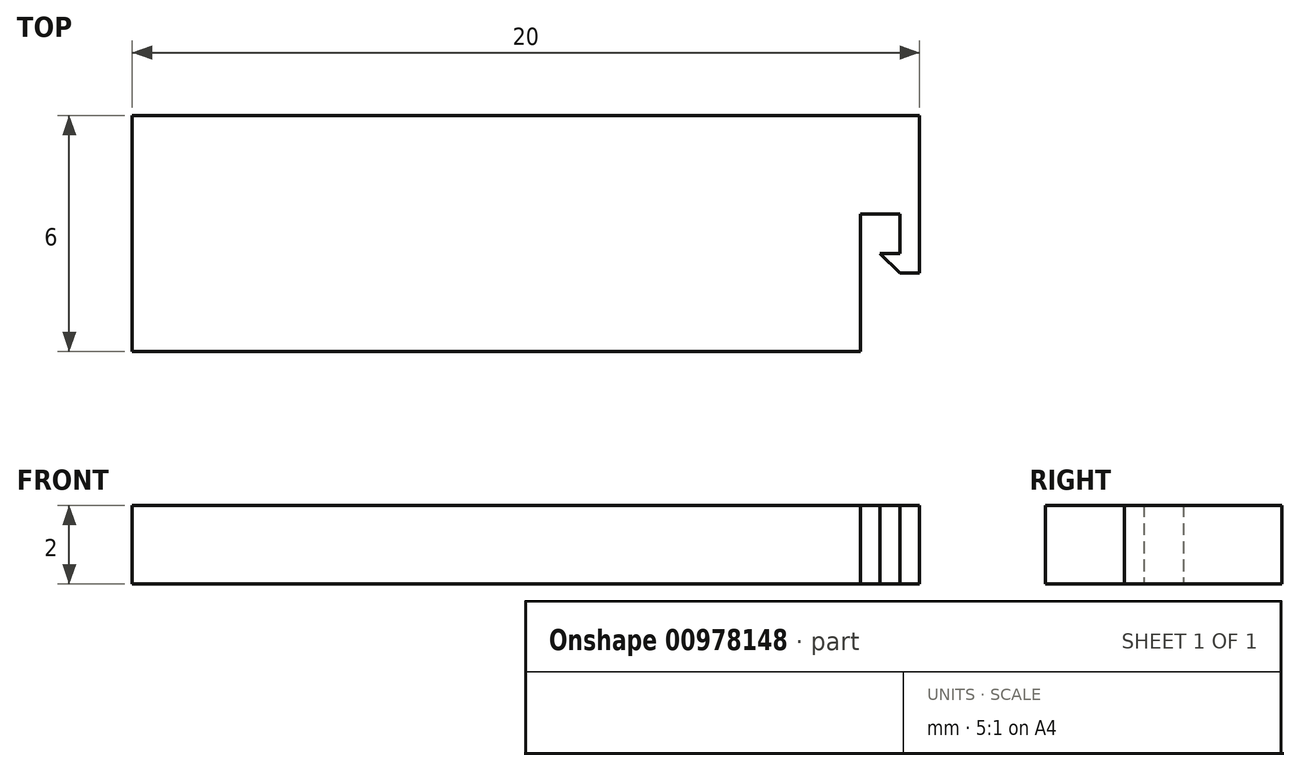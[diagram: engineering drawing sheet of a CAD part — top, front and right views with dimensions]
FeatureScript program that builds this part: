
annotation { "Feature Type Name" : "Feature", "Feature Type Description" : "" }
export const myFeature = defineFeature(function(context is Context, id is Id, definition is map)
    precondition{}
    {
        {
            var Q0;
            Q0=qCreatedBy(makeId("Top.planeOp"),FACE);
            var sketch = newSketch(context, id + "F0", { "sketchPlane" : qUnion([Q0])});
            skLineSegment(sketch, "E0.top", {"start": v(10, 3) * mm, "end": v(-10, 3) * mm});
            skLineSegment(sketch, "E0.left", {"start": v(10, -1) * mm, "end": v(10, 3) * mm});
            skLineSegment(sketch, "E0.right", {"start": v(-10, -3) * mm, "end": v(-10, 3) * mm});
            skPoint(sketch, "E0.middle", {"position": v(0, 0) * mm});
            skLineSegment(sketch, "E1.bottom", {"start": v(9.5, -0.5) * mm, "end": v(9, -0.5) * mm});
            skLineSegment(sketch, "E1.top", {"start": v(9.5, 0.5) * mm, "end": v(9, 0.5) * mm});
            skLineSegment(sketch, "E1.left", {"start": v(9.5, -0.5) * mm, "end": v(9.5, 0.5) * mm});
            skLineSegment(sketch, "E1.right", {"start": v(8.5, -0.5) * mm, "end": v(8.5, 0.5) * mm});
            skPoint(sketch, "E1.middle", {"position": v(9, 0) * mm});
            skPoint(sketch, "E2.oppositeSnap0", {"position": v(9, 0.5) * mm});
            skLineSegment(sketch, "E2.left", {"start": v(8.5, -3) * mm, "end": v(8.5, 0.5) * mm});
            skLineSegment(sketch, "E3.trimOffspring", {"start": v(8.5, -3) * mm, "end": v(-10, -3) * mm});
            skLineSegment(sketch, "E4", {"start": v(9, -0.5) * mm, "end": v(9.5, -1) * mm});
            skLineSegment(sketch, "E5", {"start": v(9.5, -1) * mm, "end": v(10, -1) * mm});
            skPoint(sketch, "E0.bottom.start.orphan", {"position": v(10, -3) * mm});
            skLineSegment(sketch, "E6", {"start": v(8.5, 0.5) * mm, "end": v(9, 0.5) * mm});
            skPoint(sketch, "E2.top.end.orphan", {"position": v(9, 1.5) * mm});
            skSolve(sketch);
        }
        {
            var Q0;
            Q0 = qSketchRegion(id + "F0", true);
            extrude(context, id + "F1", {"entities" : qUnion([Q0]), "depth" : 2 * mm, "offsetDistance" : 25 * mm});
        }
    });
